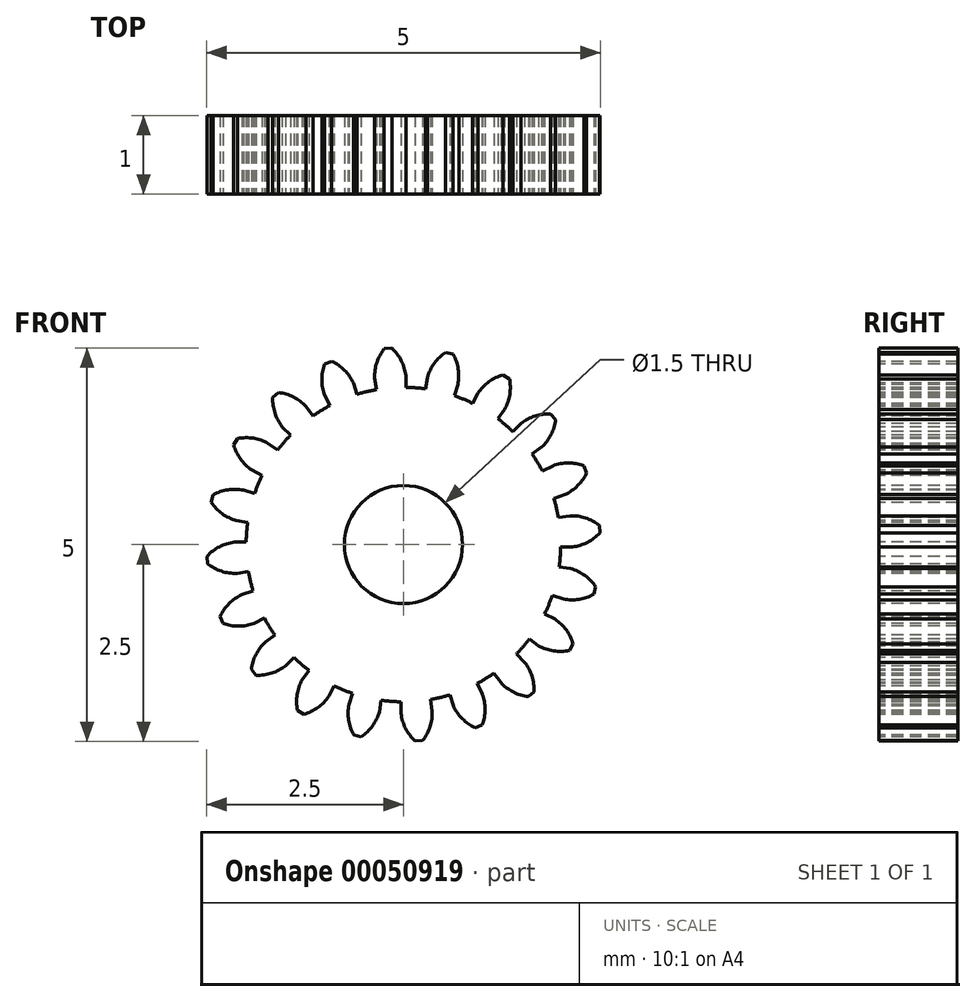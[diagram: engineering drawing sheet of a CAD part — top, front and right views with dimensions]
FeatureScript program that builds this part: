
annotation { "Feature Type Name" : "Feature", "Feature Type Description" : "" }
export const myFeature = defineFeature(function(context is Context, id is Id, definition is map)
    precondition{}
    {
        {
            assignVariable(context, id + "F0", {"name" : "N", "anyValue" : 20});
        }
        {
            var Q0;
            Q0=qCreatedBy(makeId("Front.planeOp"),FACE);
            var sketch = newSketch(context, id + "F1", { "sketchPlane" : qUnion([Q0])});
            skCircle(sketch, "E0", {"center": v(0, 0) * mm, "radius": 2.5 * mm, "construction": true});
            skCircle(sketch, "E1", {"center": v(0, 0) * mm, "radius": 2.27 * mm, "construction": true});
            skCircle(sketch, "E2", {"center": v(0, 0) * mm, "radius": 2 * mm});
            skLineSegment(sketch, "E3", {"start": v(0, 0) * mm, "end": v(0, 3.3) * mm, "construction": true});
            skLineSegment(sketch, "E4", {"start": v(0, 0) * mm, "end": v(-0.26, 3.3) * mm, "construction": true});
            skCircle(sketch, "E5", {"center": v(0, 2.27) * mm, "radius": 0.57 * mm, "construction": true});
            skArc(sketch, "E6", {"start": v(-0.15, 2.5) * mm, "mid": v(-1.07, 1.89) * mm, "end": v(0.03, 2) * mm, "construction": true});
            skPoint(sketch, "E7", {"position": v(-0.15, 2.5) * mm});
            skLineSegment(sketch, "E8", {"start": v(-0.24, 2.49) * mm, "end": v(-0.15, 2.5) * mm});
            skLineSegment(sketch, "E9", {"start": v(0, 2.27) * mm, "end": v(-1.5, 2.27) * mm, "construction": true});
            skLineSegment(sketch, "E10", {"start": v(0, 2.27) * mm, "end": v(-2.42, 1.4) * mm, "construction": true});
            skArc(sketch, "E11", {"start": v(0.03, 2.15) * mm, "mid": v(-0.03, 2.34) * mm, "end": v(-0.15, 2.5) * mm});
            skPoint(sketch, "E12", {"position": v(0.03, 2) * mm});
            skCircle(sketch, "E13", {"center": v(0, 0) * mm, "radius": 0.75 * mm});
            skPoint(sketch, "E14.orphan", {"position": v(0.03, 2.15) * mm});
            skPoint(sketch, "E15.orphan", {"position": v(-0.37, 2.11) * mm});
            skPoint(sketch, "E16.orphan", {"position": v(-0.24, 2.49) * mm});
            skCircle(sketch, "E17.converted", {"center": v(0, 0) * mm, "radius": 2.15 * mm, "construction": true});
            skLineSegment(sketch, "E18", {"start": v(0.03, 2.15) * mm, "end": v(0.03, 2) * mm});
            skArc(sketch, "E19.MirrorCS", {"start": v(-0.37, 2.11) * mm, "mid": v(-0.34, 2.31) * mm, "end": v(-0.24, 2.49) * mm});
            skLineSegment(sketch, "E20.MirrorCS", {"start": v(-0.37, 2.11) * mm, "end": v(-0.34, 1.97) * mm});
            skSolve(sketch);
        }
        {
            var Q0;
            {var subQ0=sQuery(id+"F1.wireOp",EDGE,"E2");var subQ1=makeQuery(id+"F1.imprint","INTERSECT",VERTEX,{"derivedFrom":[subQ0,sQuery(id+"F1.wireOp",EDGE,"108d931c-383f-4925-9fca-6232282d090d")]});Q0=makeQuery(id+"F1.imprint","IMPRINT",FACE,{"disambiguationData":[TD([[makeQuery(id+"F1.imprint","IMPRINT",EDGE,{"disambiguationData":[TD([[subQ1,-1.0]])],"derivedFrom":subQ0}),1.0]])]});}
            var Q1;
            Q1=makeQuery(id+"F1.imprint","IMPRINT",FACE,{"disambiguationData":[TD([[makeQuery(id+"F1.imprint","IMPRINT",EDGE,{"derivedFrom":sQuery(id+"F1.wireOp",EDGE,"E8")}),-1.0]])]});
            extrude(context, id + "F2", {"entities" : qUnion([Q0, Q1]), "oppositeDirection" : true, "depth" : 1 * mm});
        }
        {
            var Q0;
            Q0=makeQuery(id+"F2.opExtrude","SWEPT_BODY",BODY,{"disambiguationData":[OSD([sQuery(id+"F1.wireOp",EDGE,"E2"),sQuery(id+"F1.wireOp",EDGE,"E8"),sQuery(id+"F1.wireOp",EDGE,"E11"),sQuery(id+"F1.wireOp",EDGE,"7b44ec38-82ac-489c-895e-784479ee6310"),sQuery(id+"F1.wireOp",EDGE,"66a66f3c-7103-4b4e-afb5-6094ba6262ea0.MirrorCS"),sQuery(id+"F1.wireOp",EDGE,"86192332-b820-469b-9f86-a2fa7e4eb0e50.MirrorCS")])]});
            var Q1;
            Q1=sQuery(id+"F1.wireOp",EDGE,"E2");
            circularPattern(context, id + "F3", {"operationType" : NewBodyOperationType.ADD, "entities" : qUnion([Q0]), "axis" : qUnion([Q1]), "angle" : (360 / getVariable(context, 'N')) * degree, "instanceCount" : getVariable(context, 'N')});
        }
    });
